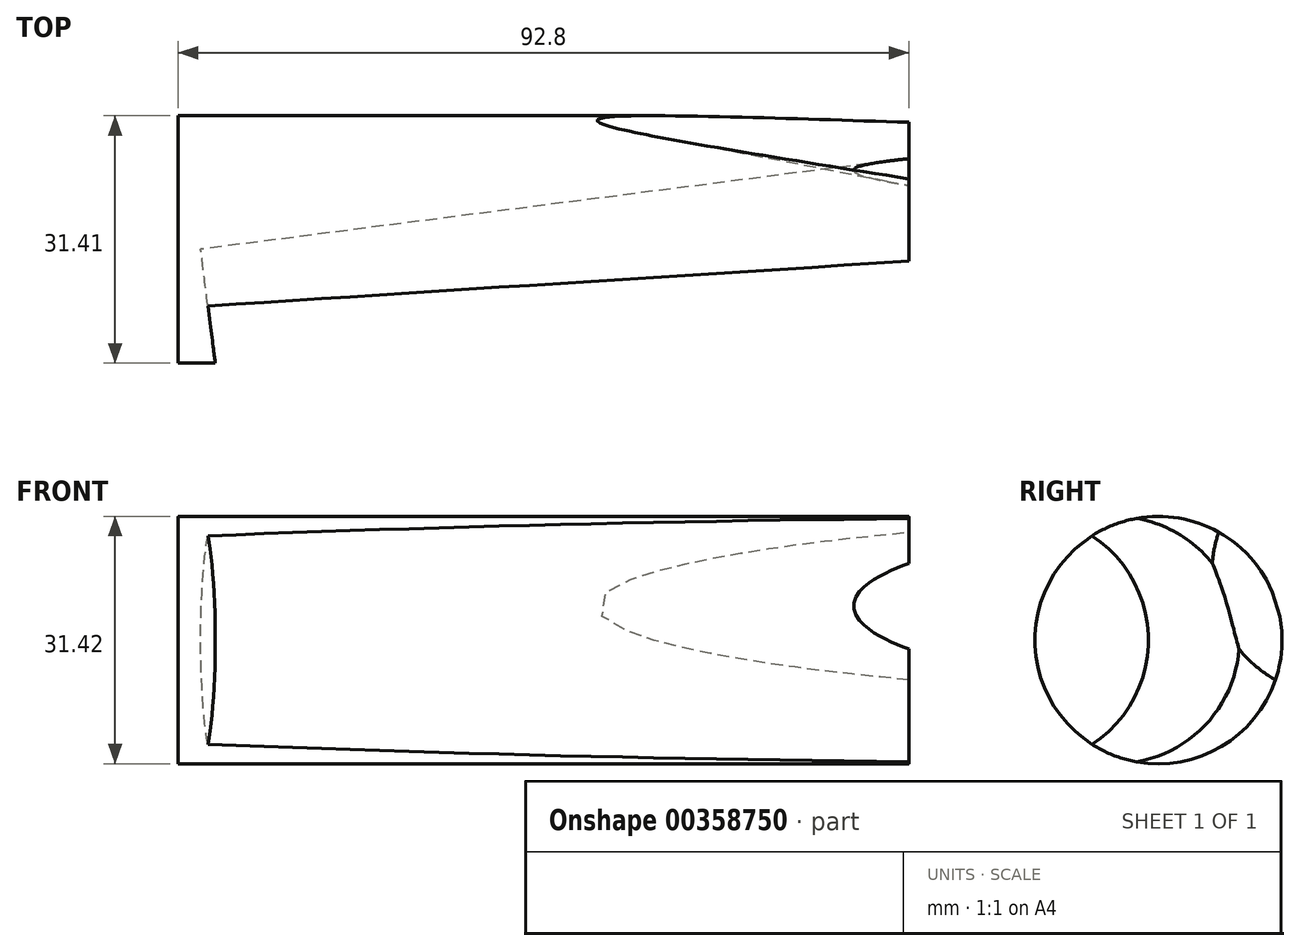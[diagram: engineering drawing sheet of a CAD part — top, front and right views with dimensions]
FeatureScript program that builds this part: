
annotation { "Feature Type Name" : "Feature", "Feature Type Description" : "" }
export const myFeature = defineFeature(function(context is Context, id is Id, definition is map)
    precondition{}
    {
        {
            var Q0;
            Q0=qCreatedBy(makeId("Right.planeOp"),FACE);
            var sketch = newSketch(context, id + "F0", { "sketchPlane" : qUnion([Q0])});
            skCircle(sketch, "E0", {"center": v(-37.14, 18.66) * mm, "radius": 15.7 * mm});
            skSolve(sketch);
        }
        {
            var Q0;
            Q0 = qSketchRegion(id + "F0", true);
            extrude(context, id + "F1", {"entities" : qUnion([Q0]), "depth" : 92.8 * mm});
        }
        {
            var Q0;
            Q0=makeQuery(id+"F1.opExtrude","SWEPT_BODY",BODY,{"disambiguationData":[OSD([sQuery(id+"F0.wireOp",EDGE,"E0")])]});
            transform(context, id + "F2", {"entities" : qUnion([Q0]), "transformType" : TransformType.TRANSLATION_3D, "dx" : 0 * mm, "dy" : 47.6 * mm, "dz" : 0 * mm, "makeCopy" : true});
        }
        {
            var Q0;
            Q0=makeQuery(id+"F2.opPattern","COPY",BODY,{"derivedFrom":makeQuery(id+"F1.opExtrude","SWEPT_BODY",BODY,{"disambiguationData":[OSD([sQuery(id+"F0.wireOp",EDGE,"E0")])]}),"instanceName":"1"});
            transform(context, id + "F3", {"entities" : qUnion([Q0]), "transformType" : TransformType.TRANSLATION_3D, "dx" : 0 * mm, "dy" : 49.9 * mm, "dz" : 0 * mm, "makeCopy" : true});
        }
        {
            var Q0;
            Q0=makeQuery(id+"F1.opExtrude","SWEPT_BODY",BODY,{"disambiguationData":[OSD([sQuery(id+"F0.wireOp",EDGE,"E0")])]});
            transform(context, id + "F4", {"entities" : qUnion([Q0]), "transformType" : TransformType.TRANSLATION_3D, "dx" : 4 * mm, "dy" : 30.2 * mm, "dz" : 0 * mm, "makeCopy" : false});
        }
        {
            var Q0;
            Q0=qCreatedBy(makeId("Right.planeOp"),FACE);
            var sketch = newSketch(context, id + "F5", { "sketchPlane" : qUnion([Q0])});
            skLineSegment(sketch, "E1", {"start": v(0, 60.09) * mm, "end": v(0, -27.06) * mm});
            skSolve(sketch);
        }
        {
            var Q0;
            Q0=makeQuery(id+"F1.opExtrude","SWEPT_BODY",BODY,{"disambiguationData":[OSD([sQuery(id+"F0.wireOp",EDGE,"E0")])]});
            var Q1;
            Q1=sQuery(id+"F5.wireOp",EDGE,"E1");
            transform(context, id + "F6", {"entities" : qUnion([Q0]), "transformType" : TransformType.ROTATION, "transformAxis" : qUnion([Q1]), "angle" : 7.3 * degree, "oppositeDirection" : true, "makeCopy" : false});
        }
        {
            var Q0;
            Q0=makeQuery(id+"F3.opPattern","COPY",BODY,{"derivedFrom":makeQuery(id+"F2.opPattern","COPY",BODY,{"derivedFrom":makeQuery(id+"F1.opExtrude","SWEPT_BODY",BODY,{"disambiguationData":[OSD([sQuery(id+"F0.wireOp",EDGE,"E0")])]}),"instanceName":"1"}),"instanceName":"1"});
            transform(context, id + "F7", {"entities" : qUnion([Q0]), "transformType" : TransformType.TRANSLATION_3D, "dx" : 2.4 * mm, "dy" : 0 * mm, "dz" : 0 * mm, "makeCopy" : false});
        }
        {
            var Q0;
            Q0=makeQuery(id+"F3.opPattern","COPY",BODY,{"derivedFrom":makeQuery(id+"F2.opPattern","COPY",BODY,{"derivedFrom":makeQuery(id+"F1.opExtrude","SWEPT_BODY",BODY,{"disambiguationData":[OSD([sQuery(id+"F0.wireOp",EDGE,"E0")])]}),"instanceName":"1"}),"instanceName":"1"});
            transform(context, id + "F8", {"entities" : qUnion([Q0]), "transformType" : TransformType.TRANSLATION_3D, "dx" : 0 * mm, "dy" : -10 * mm, "dz" : 0 * mm, "makeCopy" : false});
        }
        {
            var Q0;
            Q0=makeQuery(id+"F3.opPattern","COPY",BODY,{"derivedFrom":makeQuery(id+"F2.opPattern","COPY",BODY,{"derivedFrom":makeQuery(id+"F1.opExtrude","SWEPT_BODY",BODY,{"disambiguationData":[OSD([sQuery(id+"F0.wireOp",EDGE,"E0")])]}),"instanceName":"1"}),"instanceName":"1"});
            transform(context, id + "F9", {"entities" : qUnion([Q0]), "transformType" : TransformType.TRANSLATION_3D, "dx" : -0.2 * mm, "dy" : 0 * mm, "dz" : 8.6 * mm, "makeCopy" : false});
        }
        {
            var Q0;
            Q0=makeQuery(id+"F3.opPattern","COPY",BODY,{"derivedFrom":makeQuery(id+"F2.opPattern","COPY",BODY,{"derivedFrom":makeQuery(id+"F1.opExtrude","SWEPT_BODY",BODY,{"disambiguationData":[OSD([sQuery(id+"F0.wireOp",EDGE,"E0")])]}),"instanceName":"1"}),"instanceName":"1"});
            var Q1;
            Q1=sQuery(id+"F5.wireOp",EDGE,"E1");
            transform(context, id + "F10", {"entities" : qUnion([Q0]), "transformType" : TransformType.ROTATION, "transformAxis" : qUnion([Q1]), "angle" : 11 * degree, "makeCopy" : false});
        }
        {
            var Q0;
            Q0=makeQuery(id+"F1.opExtrude","SWEPT_BODY",BODY,{"disambiguationData":[OSD([sQuery(id+"F0.wireOp",EDGE,"E0")])]});
            var Q1;
            Q1=makeQuery(id+"F3.opPattern","COPY",BODY,{"derivedFrom":makeQuery(id+"F2.opPattern","COPY",BODY,{"derivedFrom":makeQuery(id+"F1.opExtrude","SWEPT_BODY",BODY,{"disambiguationData":[OSD([sQuery(id+"F0.wireOp",EDGE,"E0")])]}),"instanceName":"1"}),"instanceName":"1"});
            var Q2;
            Q2=makeQuery(id+"F2.opPattern","COPY",BODY,{"derivedFrom":makeQuery(id+"F1.opExtrude","SWEPT_BODY",BODY,{"disambiguationData":[OSD([sQuery(id+"F0.wireOp",EDGE,"E0")])]}),"instanceName":"1"});
            booleanBodies(context, id + "F11", {"operationType" : BooleanOperationType.SUBTRACTION, "tools" : qUnion([Q0, Q1]), "targets" : qUnion([Q2])});
        }
    });
